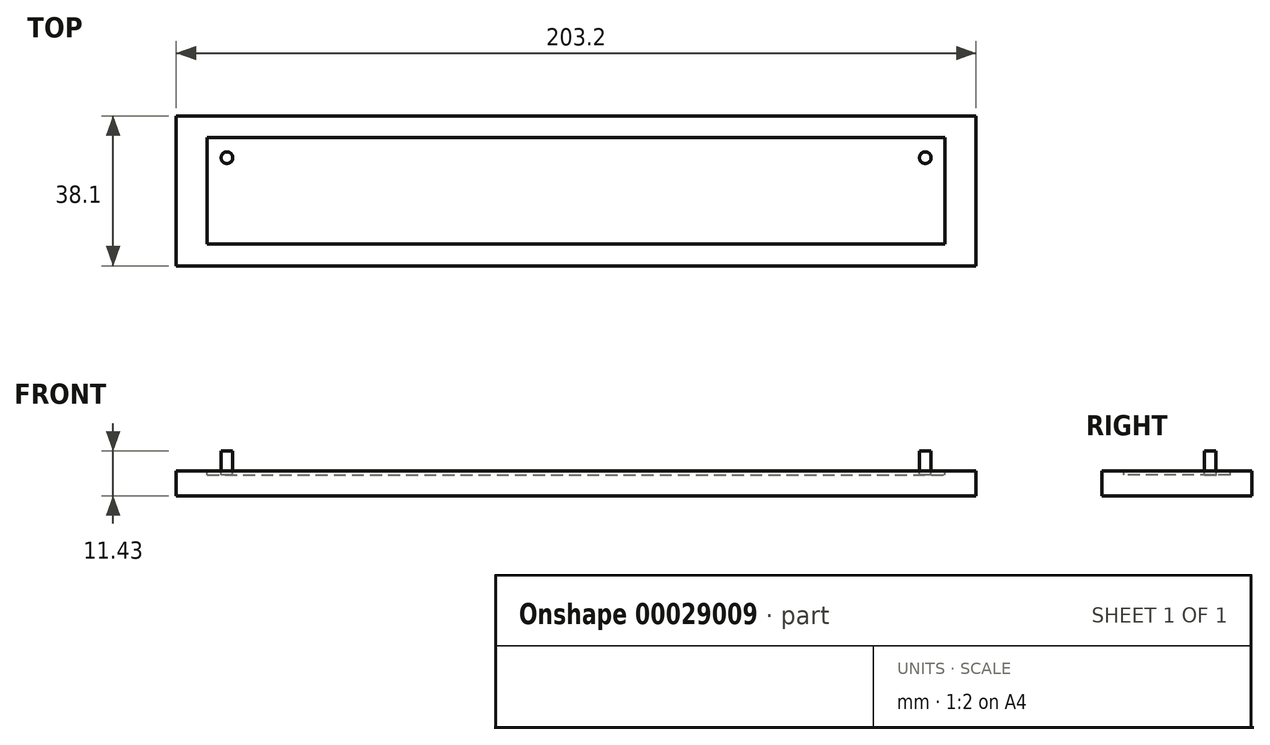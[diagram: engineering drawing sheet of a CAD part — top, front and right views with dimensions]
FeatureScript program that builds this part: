
annotation { "Feature Type Name" : "Feature", "Feature Type Description" : "" }
export const myFeature = defineFeature(function(context is Context, id is Id, definition is map)
    precondition{}
    {
        {
            var Q0;
            Q0=qCreatedBy(makeId("Top.planeOp"),FACE);
            var sketch = newSketch(context, id + "F0", { "sketchPlane" : qUnion([Q0])});
            skLineSegment(sketch, "E0.rect.bottom", {"start": v(-101.6, 19.05) * mm, "end": v(101.6, 19.05) * mm});
            skLineSegment(sketch, "E0.rect.top", {"start": v(-101.6, -19.05) * mm, "end": v(101.6, -19.05) * mm});
            skLineSegment(sketch, "E0.rect.left", {"start": v(-101.6, 19.05) * mm, "end": v(-101.6, -19.05) * mm});
            skLineSegment(sketch, "E0.rect.right", {"start": v(101.6, 19.05) * mm, "end": v(101.6, -19.05) * mm});
            skPoint(sketch, "E0.rect.middle", {"position": v(0, 0) * mm});
            skSolve(sketch);
        }
        {
            var Q0;
            Q0 = qSketchRegion(id + "F0", true);
            extrude(context, id + "F1", {"entities" : qUnion([Q0]), "depth" : 6.35 * mm});
        }
        {
            var Q0;
            Q0=makeQuery(id+"F1.opExtrude","CAP_FACE",FACE,{"disambiguationData":[OSD([sQuery(id+"F0.wireOp",EDGE,"E0.rect.bottom"),sQuery(id+"F0.wireOp",EDGE,"E0.rect.top"),sQuery(id+"F0.wireOp",EDGE,"E0.rect.left"),sQuery(id+"F0.wireOp",EDGE,"E0.rect.right")])],"isStart":false});
            var sketch = newSketch(context, id + "F2", { "sketchPlane" : qUnion([Q0])});
            skLineSegment(sketch, "E1.rect.bottom", {"start": v(-93.75, 13.54) * mm, "end": v(93.75, 13.54) * mm});
            skLineSegment(sketch, "E1.rect.top", {"start": v(-93.75, -13.54) * mm, "end": v(93.75, -13.54) * mm});
            skLineSegment(sketch, "E1.rect.left", {"start": v(-93.75, 13.54) * mm, "end": v(-93.75, -13.54) * mm});
            skLineSegment(sketch, "E1.rect.right", {"start": v(93.75, 13.54) * mm, "end": v(93.75, -13.54) * mm});
            skPoint(sketch, "E1.rect.middle", {"position": v(0, 0) * mm});
            skCircle(sketch, "E2", {"center": v(-88.7, 8.46) * mm, "radius": 1.49 * mm});
            skCircle(sketch, "E3", {"center": v(88.7, 8.46) * mm, "radius": 1.49 * mm});
            skSolve(sketch);
        }
        {
            var Q0;
            Q0 = qSketchRegion(id + "F2", true);
            extrude(context, id + "F3", {"entities" : qUnion([Q0]), "operationType" : NewBodyOperationType.REMOVE, "oppositeDirection" : true, "depth" : 1.02 * mm});
        }
        {
            var Q0;
            Q0=makeQuery(id+"F3.boolean.opBoolean","SPLIT",FACE,{"disambiguationData":[TD([makeQuery(id+"F3.opExtrude","SWEPT_FACE",FACE,{"disambiguationData":[OSD([sQuery(id+"F2.wireOp",EDGE,"E3")])]})])],"derivedFrom":makeQuery(id+"F1.opExtrude","CAP_FACE",FACE,{"disambiguationData":[OSD([sQuery(id+"F0.wireOp",EDGE,"E0.rect.bottom"),sQuery(id+"F0.wireOp",EDGE,"E0.rect.top"),sQuery(id+"F0.wireOp",EDGE,"E0.rect.left"),sQuery(id+"F0.wireOp",EDGE,"E0.rect.right")])],"isStart":false})});
            var sketch = newSketch(context, id + "F4", { "sketchPlane" : qUnion([Q0])});
            skCircle(sketch, "E4", {"center": v(88.7, 8.46) * mm, "radius": 1.47 * mm});
            skCircle(sketch, "E5", {"center": v(-88.7, 8.46) * mm, "radius": 1.47 * mm});
            skSolve(sketch);
        }
        {
            var Q0;
            Q0 = qSketchRegion(id + "F4", true);
            extrude(context, id + "F5", {"entities" : qUnion([Q0]), "operationType" : NewBodyOperationType.ADD, "depth" : 5.08 * mm});
        }
    });
